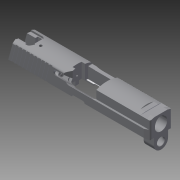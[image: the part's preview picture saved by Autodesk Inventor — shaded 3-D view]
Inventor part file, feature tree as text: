
AUTODESK INVENTOR PART (.ipt)
format: ipt  version: 2014 SP2 (Build 180246200, 246)  size: 1,582,592 bytes
history: native  units: in
note: dims shown in document units (in); Inventor stores cm internally (conversion verified against a paired STEP export)
features: other x3, plane x1
ambient origin geometry x8: Origin, YZ Plane, XZ Plane, XY Plane, X Axis, Y Axis, Z Axis, Center Point
bodies: Solid1 (feature_tree)
feature tree (4):
  other  "Slide"
  plane  "Work Plane1"
  other  "Slide::Slide"
  other  "TaggingFeature1"
